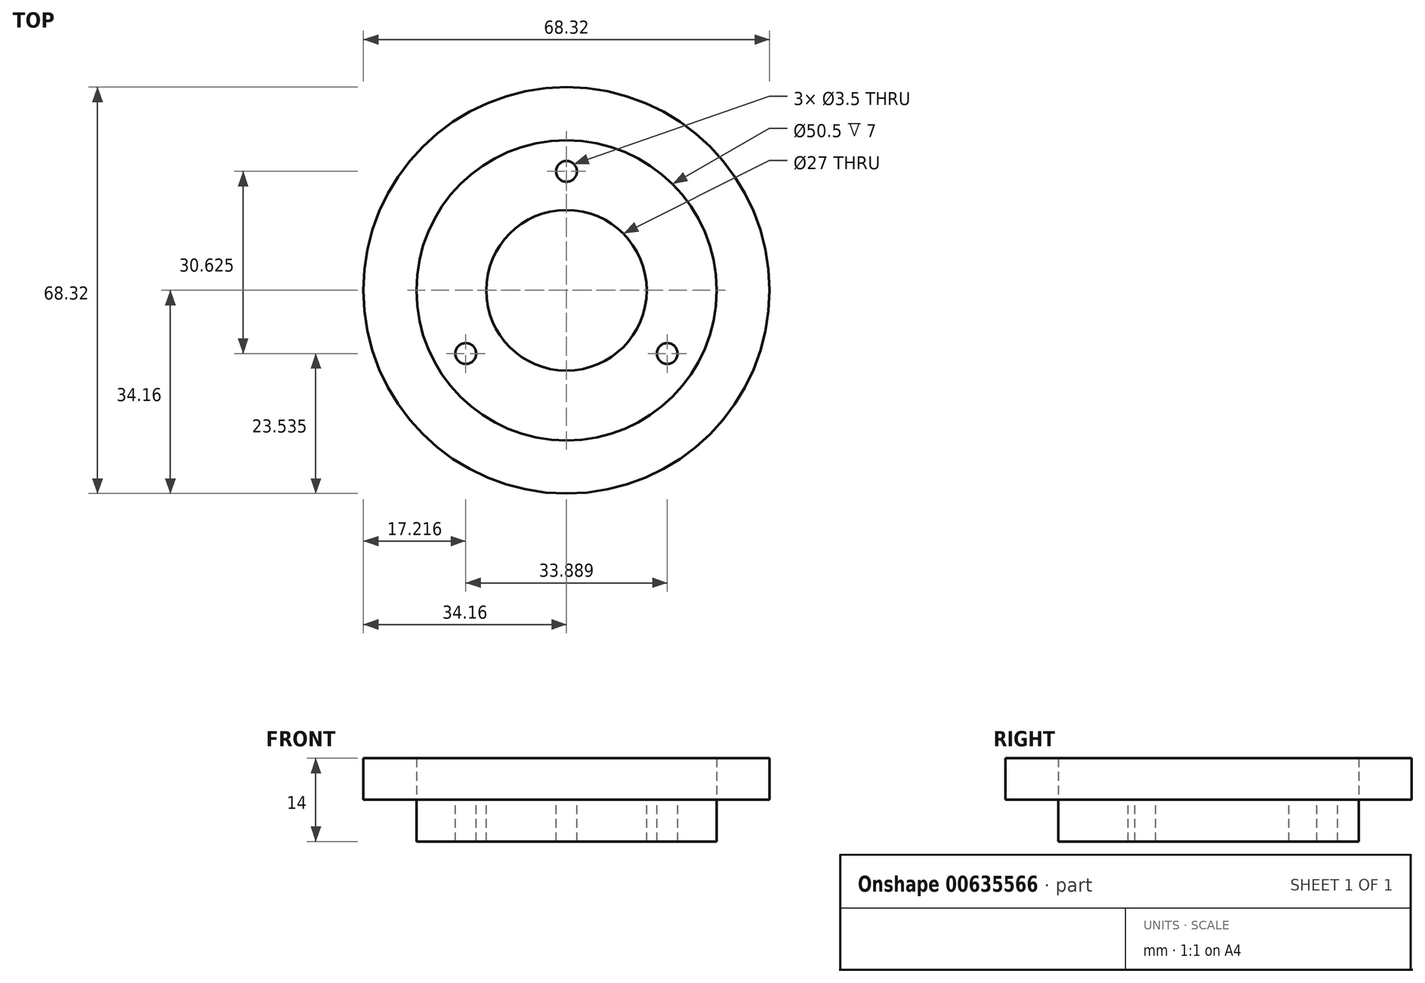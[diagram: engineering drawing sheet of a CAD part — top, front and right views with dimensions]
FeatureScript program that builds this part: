
annotation { "Feature Type Name" : "Feature", "Feature Type Description" : "" }
export const myFeature = defineFeature(function(context is Context, id is Id, definition is map)
    precondition{}
    {
        {
            var Q0;
            Q0=qCreatedBy(makeId("Top.planeOp"),FACE);
            var sketch = newSketch(context, id + "F0", { "sketchPlane" : qUnion([Q0])});
            skCircle(sketch, "E0", {"center": v(0, 0) * mm, "radius": 13.5 * mm});
            skCircle(sketch, "E1", {"center": v(0, 0) * mm, "radius": 25.25 * mm});
            skCircle(sketch, "E2", {"center": v(0, 20) * mm, "radius": 1.75 * mm});
            skCircle(sketch, "E3", {"center": v(-16.94, -10.63) * mm, "radius": 1.75 * mm});
            skCircle(sketch, "E4", {"center": v(16.94, -10.62) * mm, "radius": 1.75 * mm});
            skCircle(sketch, "E5", {"center": v(0, 0) * mm, "radius": 34.16 * mm});
            skSolve(sketch);
        }
        {
            var Q0;
            Q0=makeQuery(id+"F0.imprint","IMPRINT",FACE,{"disambiguationData":[TD([[makeQuery(id+"F0.imprint","IMPRINT",EDGE,{"derivedFrom":sQuery(id+"F0.wireOp",EDGE,"E0")}),-1.0]])]});
            extrude(context, id + "F1", {"entities" : qUnion([Q0]), "oppositeDirection" : true, "depth" : 7 * mm, "offsetDistance" : 25.4 * mm});
        }
        {
            var Q0;
            Q0=makeQuery(id+"F0.imprint","IMPRINT",FACE,{"disambiguationData":[TD([[makeQuery(id+"F0.imprint","IMPRINT",EDGE,{"derivedFrom":sQuery(id+"F0.wireOp",EDGE,"E1")}),-1.0]])]});
            var Q1;
            Q1=sQuery(id+"F0.wireOp",EDGE,"E5");
            var Q2;
            Q2=sQuery(id+"F0.wireOp",EDGE,"E1");
            extrude(context, id + "F2", {"entities" : qUnion([Q0]), "surfaceEntities" : qUnion([Q1, Q2]), "depth" : 7 * mm, "offsetDistance" : 25.4 * mm});
        }
    });
